# Revit family: DoorPanel_Aluminum_Cline_Louver-TopAndBottom
name_source: partatom
category: Doors
units: mm (PartAtom-declared; Revit-internal decimal feet)

## family parameters
Always vertical = No
Classification Number = 23.30.10.11.14
Cut with Voids When Loaded = No
Room Calculation Point = No
Shared = Yes
Work Plane-Based = No

## types (1)
- DoorPanel_Aluminum_Cline_Louver-TopAndBottom
    Base Height = 3' - 7"
    Description = Cline Aluminum Doors Door Panel - Model - 100BE
    Expected Lifespan (Years) = 0
    Function = Interior
    Installation-Fabrication = http://www.clinedoors.com
    Louver Height Bottom = 2' - 0"
    Louver Height Top = 2' - 10"
    Louver Width = 2' - 0"
    Maintenance Schedule (Months) = 0
    Manufacturer = Cline Aluminum Doors, Inc.
    Manufacturer Fax = 941-746-5153
    Manufacturer Website = http://www.clinedoors.com
    Model = 100BE
    Product Data = http://www.arcat.com
    Revision = R1_04-2012
    Sales Information = http://www.clinedoors.com
    Send Message = http://www.arcat.com Aluminum Doors, Inc.&coid=31485&rep=145&fax=941-746-5153&mf=
    Specification = http://www.arcat.com
    Test Data = http://www.clinedoors.com
    URL = http://www.clinedoors.com
    Warranty Duration (Years) = 0

## geometry (parser evidence)
native form markers: Blend x24, Sweep x6
no freeform markers — native parametric forms only
